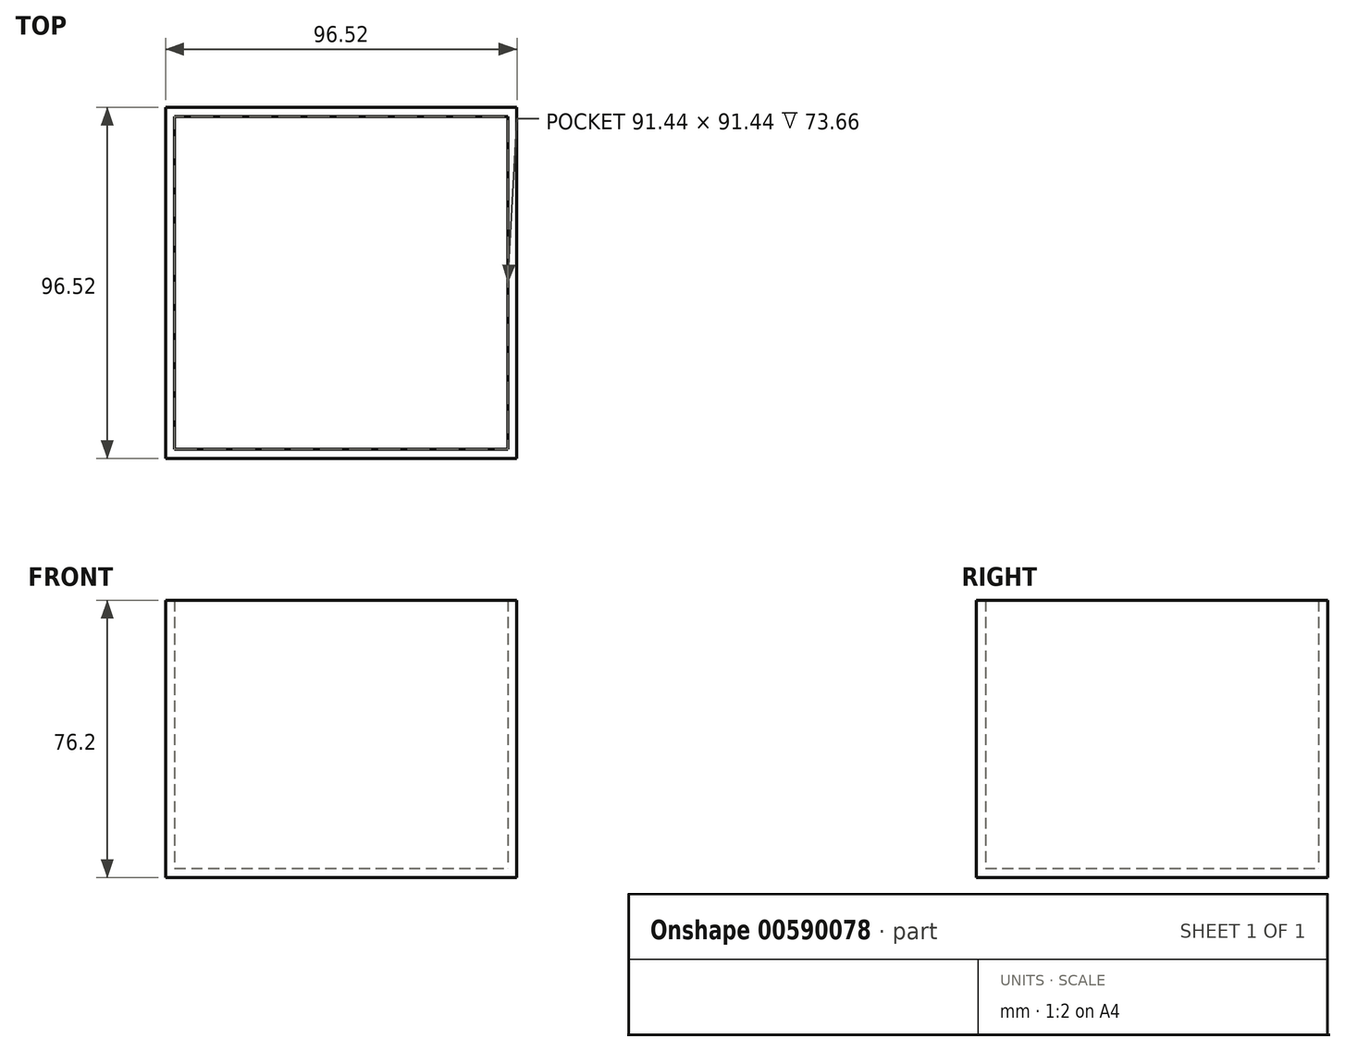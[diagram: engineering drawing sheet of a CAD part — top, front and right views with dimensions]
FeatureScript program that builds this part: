
annotation { "Feature Type Name" : "Feature", "Feature Type Description" : "" }
export const myFeature = defineFeature(function(context is Context, id is Id, definition is map)
    precondition{}
    {
        {
            var Q0;
            Q0=qCreatedBy(makeId("Front.planeOp"),FACE);
            var sketch = newSketch(context, id + "F0", { "sketchPlane" : qUnion([Q0])});
            skLineSegment(sketch, "E0.bottom", {"start": v(-42.24, 64.55) * mm, "end": v(54.28, 64.55) * mm});
            skLineSegment(sketch, "E0.top", {"start": v(-42.24, -11.65) * mm, "end": v(54.28, -11.65) * mm});
            skLineSegment(sketch, "E0.left", {"start": v(-42.24, 64.55) * mm, "end": v(-42.24, -11.65) * mm});
            skLineSegment(sketch, "E0.right", {"start": v(54.28, 64.55) * mm, "end": v(54.28, -11.65) * mm});
            skSolve(sketch);
        }
        {
            var Q0;
            Q0=makeQuery(id+"F0.imprint","IMPRINT",FACE,{"disambiguationData":[TD([[makeQuery(id+"F0.imprint","IMPRINT",EDGE,{"derivedFrom":sQuery(id+"F0.wireOp",EDGE,"E0.bottom")}),-1.0]])]});
            var Q1;
            Q1 = qSketchRegion(id + "F0", true);
            extrude(context, id + "F1", {"entities" : qUnion([Q0, Q1]), "depth" : 96.52 * mm, "offsetDistance" : 25.4 * mm});
        }
        {
            var Q0;
            Q0=makeQuery(id+"F1.opExtrude","SWEPT_FACE",FACE,{"disambiguationData":[OSD([sQuery(id+"F0.wireOp",EDGE,"E0.bottom")])]});
            shell(context, id + "F2", {"entities" : qUnion([Q0]), "thickness" : 2.54 * mm});
        }
    });
